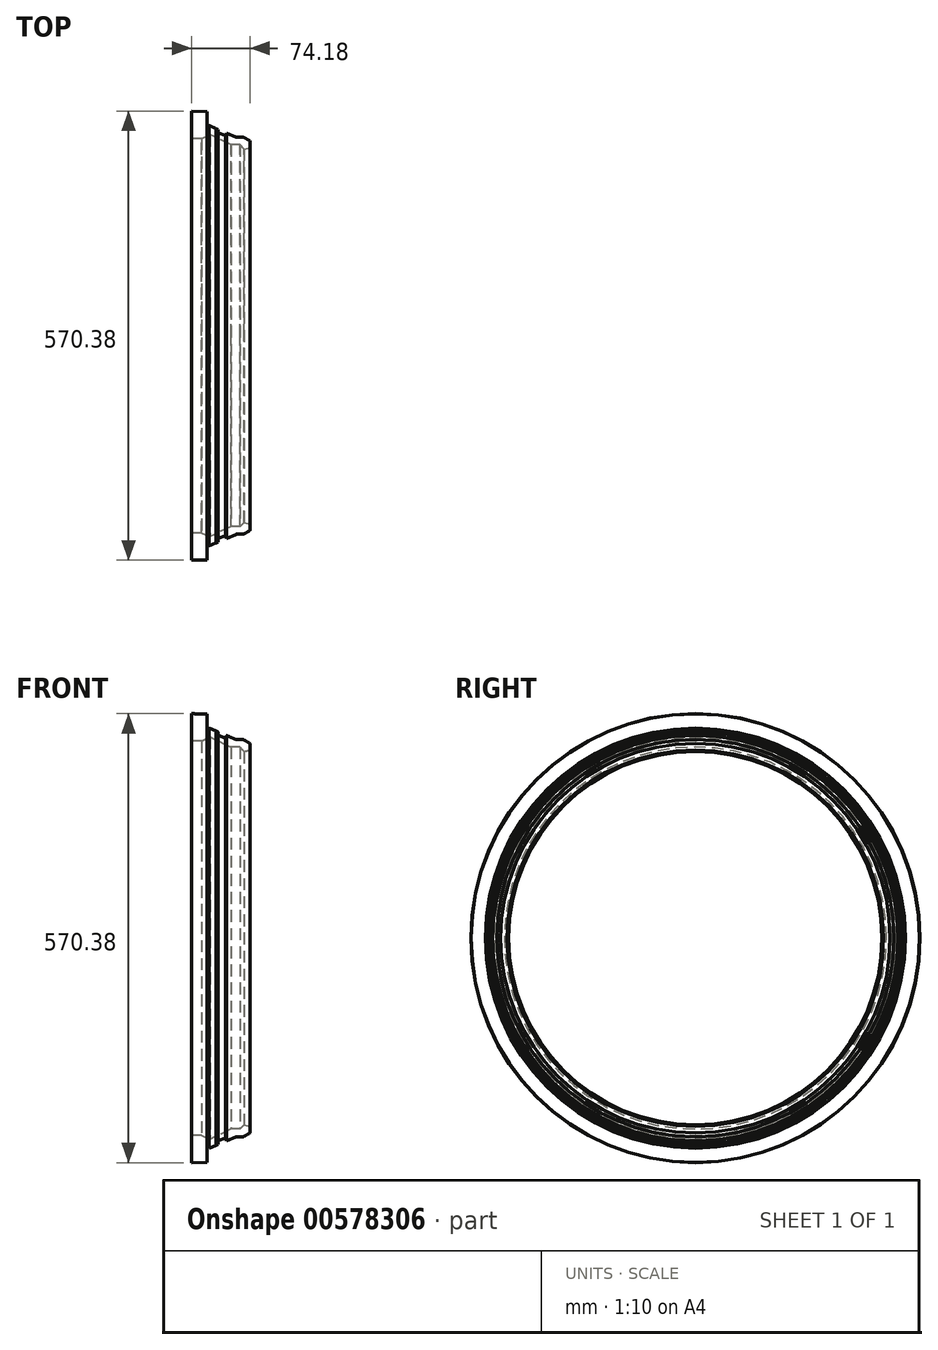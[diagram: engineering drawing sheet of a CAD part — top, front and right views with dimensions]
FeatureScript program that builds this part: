
annotation { "Feature Type Name" : "Feature", "Feature Type Description" : "" }
export const myFeature = defineFeature(function(context is Context, id is Id, definition is map)
    precondition{}
    {
        {
            var Q0;
            Q0=qCreatedBy(makeId("Front.planeOp"),FACE);
            var sketch = newSketch(context, id + "F0", { "sketchPlane" : qUnion([Q0])});
            skLineSegment(sketch, "E0", {"start": v(0, 0) * mm, "end": v(30.12, 0) * mm});
            skPoint(sketch, "E1", {"position": v(-7.36, 231.93) * mm});
            skLineSegment(sketch, "E2", {"start": v(-7.36, 237.1) * mm, "end": v(0, 239.08) * mm});
            skLineSegment(sketch, "E3.trimOffspring", {"start": v(0, 239.08) * mm, "end": v(0, 245.2) * mm});
            skLineSegment(sketch, "E4", {"start": v(-7.36, 237.1) * mm, "end": v(-12.82, 242.57) * mm});
            skLineSegment(sketch, "E5", {"start": v(-16.97, 252.22) * mm, "end": v(-8.98, 252.22) * mm});
            skLineSegment(sketch, "E6", {"start": v(-97.44, 148.32) * mm, "end": v(22.45, 148.32) * mm});
            skLineSegment(sketch, "E7", {"start": v(-97.44, 193.92) * mm, "end": v(-97.44, 70.08) * mm});
            skPoint(sketch, "E8", {"position": v(-66.59, 139.32) * mm});
            skArc(sketch, "E9", {"start": v(0, 247.47) * mm, "mid": v(-3.92, 249.79) * mm, "end": v(-7.93, 251.96) * mm});
            skLineSegment(sketch, "E10", {"start": v(0, 0) * mm, "end": v(0, 148.32) * mm});
            skArc(sketch, "E11.trimOffspring", {"start": v(-43.28, 263.2) * mm, "mid": v(-47.44, 265.06) * mm, "end": v(-51.66, 266.78) * mm});
            skLineSegment(sketch, "E12", {"start": v(-43.28, 263.2) * mm, "end": v(-40.28, 261.92) * mm});
            skLineSegment(sketch, "E13", {"start": v(-40.28, 261.92) * mm, "end": v(-41.77, 258.41) * mm});
            skLineSegment(sketch, "E14", {"start": v(-41.77, 258.41) * mm, "end": v(-31.25, 253.95) * mm});
            skLineSegment(sketch, "E15", {"start": v(-31.25, 253.95) * mm, "end": v(-29.76, 257.46) * mm});
            skLineSegment(sketch, "E16.trimOffspring", {"start": v(-29.76, 257.46) * mm, "end": v(-17.86, 252.4) * mm});
            skLineSegment(sketch, "E17.trimOffspring", {"start": v(0, 240.83) * mm, "end": v(0, 246.18) * mm});
            skLineSegment(sketch, "E18", {"start": v(-51.66, 266.78) * mm, "end": v(-52.3, 266.15) * mm});
            skLineSegment(sketch, "E19", {"start": v(-54.33, 266.06) * mm, "end": v(-52.5, 266.06) * mm});
            skLineSegment(sketch, "E20", {"start": v(-54.61, 284.8) * mm, "end": v(-54.61, 266.35) * mm});
            skLineSegment(sketch, "E21", {"start": v(-24.13, 242.57) * mm, "end": v(-13.94, 242.57) * mm});
            skPoint(sketch, "E22", {"position": v(-24.13, 242.57) * mm});
            skLineSegment(sketch, "E23", {"start": v(-13.94, 242.57) * mm, "end": v(-12.82, 242.57) * mm});
            skLineSegment(sketch, "E24", {"start": v(-24.13, 242.57) * mm, "end": v(-50.68, 255.32) * mm});
            skLineSegment(sketch, "E25", {"start": v(-50.68, 255.32) * mm, "end": v(-61.45, 250.42) * mm});
            skLineSegment(sketch, "E26", {"start": v(-61.45, 250.42) * mm, "end": v(-74.18, 250.42) * mm});
            skLineSegment(sketch, "E27", {"start": v(-74.18, 250.42) * mm, "end": v(-74.18, 285.19) * mm});
            skLineSegment(sketch, "E28", {"start": v(-74.18, 285.19) * mm, "end": v(-54.61, 284.8) * mm});
            skPoint(sketch, "E29.visualSharp", {"position": v(0, 247.47) * mm});
            skPoint(sketch, "E30.visualSharp", {"position": v(0, 239.08) * mm});
            skPoint(sketch, "E31.visualSharp", {"position": v(-8.43, 252.22) * mm});
            skArc(sketch, "E31.filletArc", {"start": v(-7.93, 251.96) * mm, "mid": v(-8.44, 252.16) * mm, "end": v(-8.98, 252.22) * mm});
            skPoint(sketch, "E32.visualSharp", {"position": v(-17.43, 252.22) * mm});
            skArc(sketch, "E32.filletArc", {"start": v(-17.86, 252.4) * mm, "mid": v(-17.42, 252.27) * mm, "end": v(-16.97, 252.22) * mm});
            skPoint(sketch, "E33.visualSharp", {"position": v(-51.66, 266.78) * mm});
            skPoint(sketch, "E34.visualSharp", {"position": v(-52.38, 266.06) * mm});
            skArc(sketch, "E34.filletArc", {"start": v(-52.5, 266.06) * mm, "mid": v(-52.4, 266.09) * mm, "end": v(-52.3, 266.15) * mm});
            skPoint(sketch, "E35.visualSharp", {"position": v(-54.61, 266.06) * mm});
            skArc(sketch, "E35.filletArc", {"start": v(-54.61, 266.35) * mm, "mid": v(-54.53, 266.15) * mm, "end": v(-54.33, 266.06) * mm});
            skPoint(sketch, "E36.visualSharp", {"position": v(-7.36, 237.1) * mm});
            skLineSegment(sketch, "E37", {"start": v(0, 246.18) * mm, "end": v(0, 247.47) * mm});
            skSolve(sketch);
        }
        {
            var Q0;
            Q0=qSketchRegion(id+"F0",true);
            var Q1;
            Q1=sQuery(id+"F0.wireOp",EDGE,"E0");
            revolve(context, id + "F1", {"entities" : qUnion([Q0]), "axis" : qUnion([Q1]), "revolveType" : RevolveType.FULL});
        }
    });
